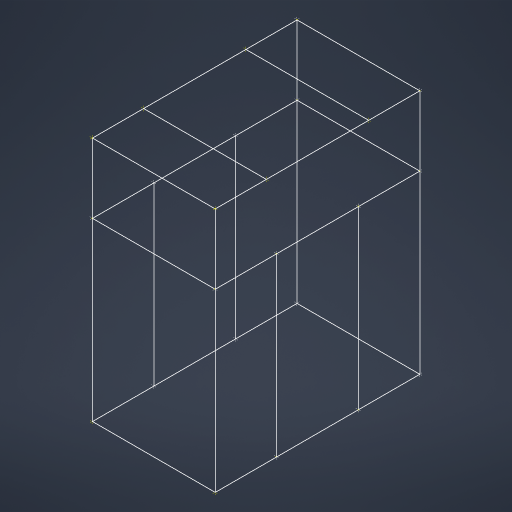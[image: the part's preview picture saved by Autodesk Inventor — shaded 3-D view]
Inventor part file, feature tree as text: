
AUTODESK INVENTOR PART (.ipt)
format: ipt  version: 2024.1 (Build 281209000, 209)  size: 198,144 bytes
history: native  units: mm
features: sketch x11, plane x4
ambient origin geometry x8: Origin, YZ Plane, XZ Plane, XY Plane, X Axis, Y Axis, Z Axis, Center Point
feature tree (15):
  sketch  "Sketch1"  dims[d0=600.0mm]
  sketch  "3D Sketch1"
  plane  "Work Plane1"
  sketch  "Sketch2"  dims[d1=1000.0mm]
  sketch  "3D Sketch2"
  sketch  "3D Sketch4"
  plane  "Work Plane2"
  sketch  "Sketch3"  dims[d2=0.0mm]
  sketch  "3D Sketch5"
  plane  "Work Plane3"
  sketch  "Sketch4"  dims[d3=1200.0mm]
  sketch  "3D Sketch6"
  plane  "Work Plane4"
  sketch  "Sketch5"  dims[d4=500.0mm d5=-340.0mm d6=400.0mm]
  sketch  "3D Sketch7"
